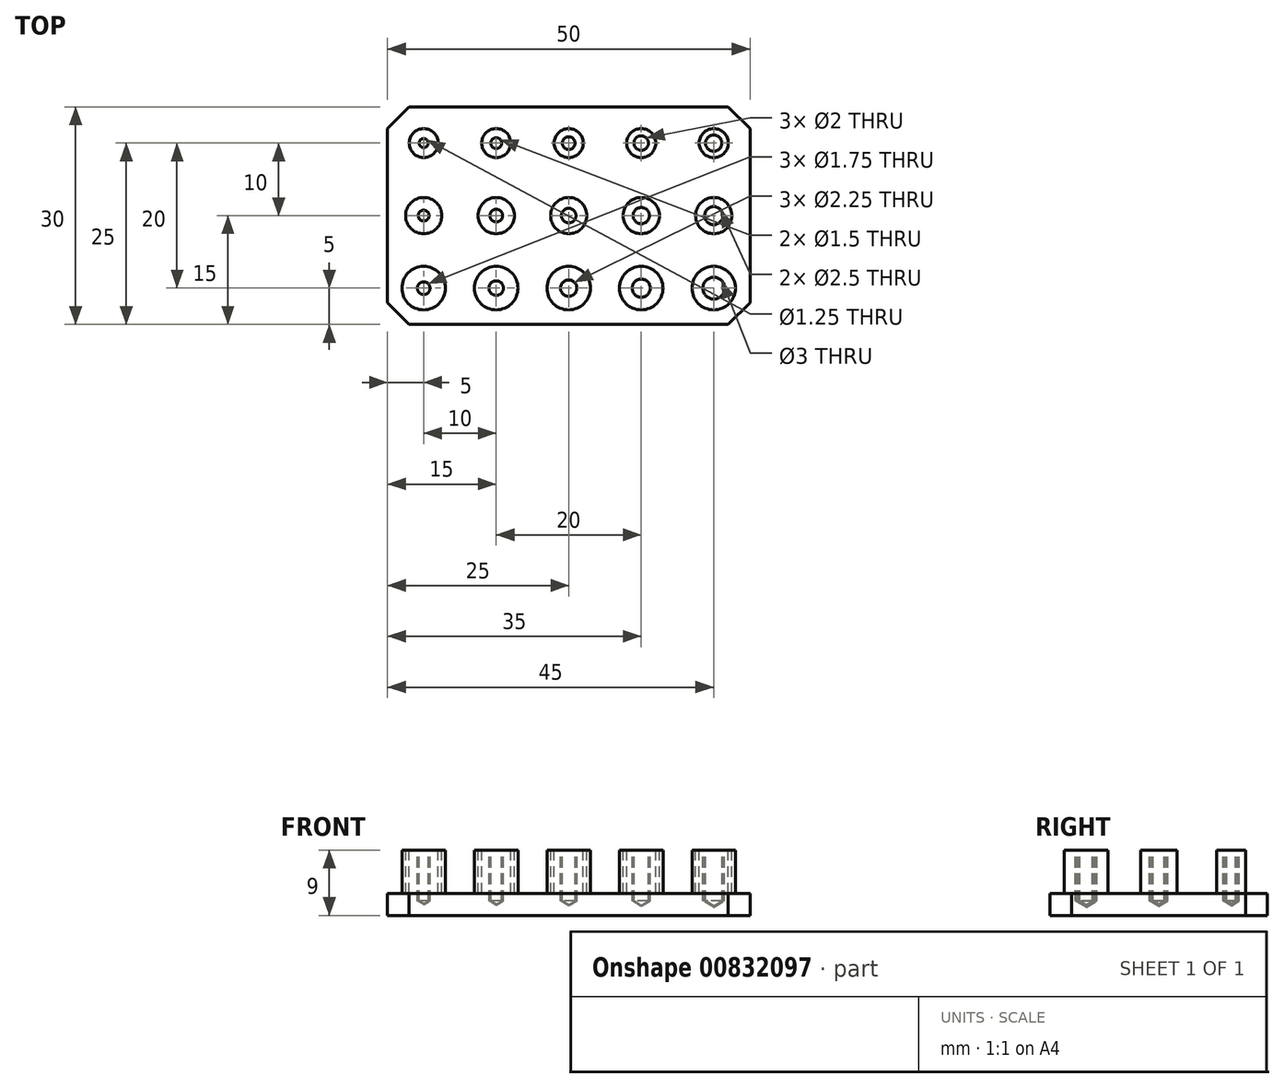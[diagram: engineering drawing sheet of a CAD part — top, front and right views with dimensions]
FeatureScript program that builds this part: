
annotation { "Feature Type Name" : "Feature", "Feature Type Description" : "" }
export const myFeature = defineFeature(function(context is Context, id is Id, definition is map)
    precondition{}
    {
        {
            var Q0;
            Q0=qCreatedBy(makeId("Top.planeOp"),FACE);
            var sketch = newSketch(context, id + "F0", { "sketchPlane" : qUnion([Q0])});
            skLineSegment(sketch, "E0.bottom", {"start": v(-25, 15) * mm, "end": v(25, 15) * mm});
            skLineSegment(sketch, "E0.top", {"start": v(-25, -15) * mm, "end": v(25, -15) * mm});
            skLineSegment(sketch, "E0.left", {"start": v(-25, 15) * mm, "end": v(-25, -15) * mm});
            skLineSegment(sketch, "E0.right", {"start": v(25, 15) * mm, "end": v(25, -15) * mm});
            skSolve(sketch);
        }
        {
            var Q0;
            Q0=makeQuery(id+"F0.imprint","IMPRINT",FACE,{"disambiguationData":[TD([[makeQuery(id+"F0.imprint","IMPRINT",EDGE,{"derivedFrom":sQuery(id+"F0.wireOp",EDGE,"E0.bottom")}),-1.0]])]});
            extrude(context, id + "F1", {"entities" : qUnion([Q0]), "oppositeDirection" : true, "depth" : 3 * mm, "offsetDistance" : 25 * mm});
        }
        {
            var Q0;
            Q0=makeQuery(id+"F1.opExtrude","SWEPT_EDGE",EDGE,{"disambiguationData":[OSD([sQuery(id+"F0.wireOp",EDGE,"E0.top"),sQuery(id+"F0.wireOp",EDGE,"E0.left")])]});
            var Q1;
            Q1=makeQuery(id+"F1.opExtrude","SWEPT_EDGE",EDGE,{"disambiguationData":[OSD([sQuery(id+"F0.wireOp",EDGE,"E0.top"),sQuery(id+"F0.wireOp",EDGE,"E0.right")])]});
            var Q2;
            Q2=makeQuery(id+"F1.opExtrude","SWEPT_EDGE",EDGE,{"disambiguationData":[OSD([sQuery(id+"F0.wireOp",EDGE,"E0.bottom"),sQuery(id+"F0.wireOp",EDGE,"E0.right")])]});
            var Q3;
            Q3=makeQuery(id+"F1.opExtrude","SWEPT_EDGE",EDGE,{"disambiguationData":[OSD([sQuery(id+"F0.wireOp",EDGE,"E0.bottom"),sQuery(id+"F0.wireOp",EDGE,"E0.left")])]});
            chamfer(context, id + "F2", {"entities" : qUnion([Q0, Q1, Q2, Q3]), "width" : 3 * mm, "tangentPropagation" : true});
        }
        {
            var Q0;
            Q0=makeQuery(id+"F1.opExtrude","CAP_FACE",FACE,{"disambiguationData":[OSD([sQuery(id+"F0.wireOp",EDGE,"E0.bottom"),sQuery(id+"F0.wireOp",EDGE,"E0.top"),sQuery(id+"F0.wireOp",EDGE,"E0.left"),sQuery(id+"F0.wireOp",EDGE,"E0.right")])],"isStart":true});
            cPlane(context, id + "F3", {"entities" : qUnion([Q0]), "cplaneType" : CPlaneType.OFFSET, "offset" : 6 * mm, "width" : 150 * mm, "height" : 150 * mm});
        }
        {
            var Q0;
            Q0=qCreatedBy(id+"F3.planeOp",FACE);
            var sketch = newSketch(context, id + "F4", { "sketchPlane" : qUnion([Q0])});
            skPoint(sketch, "E1", {"position": v(10, 0) * mm});
            skPoint(sketch, "E2", {"position": v(20, 0) * mm});
            skPoint(sketch, "E3", {"position": v(0, 0) * mm});
            skPoint(sketch, "E4", {"position": v(-10, 0) * mm});
            skPoint(sketch, "E5", {"position": v(-20, 0) * mm});
            skPoint(sketch, "E6", {"position": v(0, 10) * mm});
            skPoint(sketch, "E7", {"position": v(-10, 10) * mm});
            skPoint(sketch, "E8", {"position": v(-20, 10) * mm});
            skPoint(sketch, "E9", {"position": v(10, 10) * mm});
            skPoint(sketch, "E10", {"position": v(20, 10) * mm});
            skPoint(sketch, "E11", {"position": v(0, -10) * mm});
            skPoint(sketch, "E12", {"position": v(-10, -10) * mm});
            skPoint(sketch, "E13", {"position": v(-20, -10) * mm});
            skPoint(sketch, "E14", {"position": v(10, -10) * mm});
            skPoint(sketch, "E15", {"position": v(20, -10) * mm});
            skCircle(sketch, "E16", {"center": v(-20, 10) * mm, "radius": 2 * mm});
            skCircle(sketch, "E17", {"center": v(-10, 10) * mm, "radius": 2 * mm});
            skCircle(sketch, "E18", {"center": v(0, 10) * mm, "radius": 2 * mm});
            skCircle(sketch, "E19", {"center": v(10, 10) * mm, "radius": 2 * mm});
            skCircle(sketch, "E20", {"center": v(20, 10) * mm, "radius": 2 * mm});
            skCircle(sketch, "E21", {"center": v(-20, 0) * mm, "radius": 2.5 * mm});
            skCircle(sketch, "E22", {"center": v(-10, 0) * mm, "radius": 2.5 * mm});
            skCircle(sketch, "E23", {"center": v(0, 0) * mm, "radius": 2.5 * mm});
            skCircle(sketch, "E24", {"center": v(10, 0) * mm, "radius": 2.5 * mm});
            skCircle(sketch, "E25", {"center": v(20, 0) * mm, "radius": 2.5 * mm});
            skCircle(sketch, "E26", {"center": v(-20, -10) * mm, "radius": 3 * mm});
            skCircle(sketch, "E27", {"center": v(-10, -10) * mm, "radius": 3 * mm});
            skCircle(sketch, "E28", {"center": v(0, -10) * mm, "radius": 3 * mm});
            skCircle(sketch, "E29", {"center": v(10, -10) * mm, "radius": 3 * mm});
            skCircle(sketch, "E30", {"center": v(20, -10) * mm, "radius": 3 * mm});
            skSolve(sketch);
        }
        {
            var Q0;
            Q0=makeQuery(id+"F4.imprint","IMPRINT",FACE,{"disambiguationData":[TD([[makeQuery(id+"F4.imprint","IMPRINT",EDGE,{"derivedFrom":sQuery(id+"F4.wireOp",EDGE,"E21")}),1.0]])]});
            var Q1;
            Q1=makeQuery(id+"F4.imprint","IMPRINT",FACE,{"disambiguationData":[TD([[makeQuery(id+"F4.imprint","IMPRINT",EDGE,{"derivedFrom":sQuery(id+"F4.wireOp",EDGE,"E22")}),1.0]])]});
            var Q2;
            Q2=makeQuery(id+"F4.imprint","IMPRINT",FACE,{"disambiguationData":[TD([[makeQuery(id+"F4.imprint","IMPRINT",EDGE,{"derivedFrom":sQuery(id+"F4.wireOp",EDGE,"E23")}),1.0]])]});
            var Q3;
            Q3=makeQuery(id+"F4.imprint","IMPRINT",FACE,{"disambiguationData":[TD([[makeQuery(id+"F4.imprint","IMPRINT",EDGE,{"derivedFrom":sQuery(id+"F4.wireOp",EDGE,"E24")}),1.0]])]});
            var Q4;
            Q4=makeQuery(id+"F4.imprint","IMPRINT",FACE,{"disambiguationData":[TD([[makeQuery(id+"F4.imprint","IMPRINT",EDGE,{"derivedFrom":sQuery(id+"F4.wireOp",EDGE,"E25")}),1.0]])]});
            var Q5;
            Q5=makeQuery(id+"F4.imprint","IMPRINT",FACE,{"disambiguationData":[TD([[makeQuery(id+"F4.imprint","IMPRINT",EDGE,{"derivedFrom":sQuery(id+"F4.wireOp",EDGE,"E16")}),1.0]])]});
            var Q6;
            Q6=makeQuery(id+"F4.imprint","IMPRINT",FACE,{"disambiguationData":[TD([[makeQuery(id+"F4.imprint","IMPRINT",EDGE,{"derivedFrom":sQuery(id+"F4.wireOp",EDGE,"E17")}),1.0]])]});
            var Q7;
            Q7=makeQuery(id+"F4.imprint","IMPRINT",FACE,{"disambiguationData":[TD([[makeQuery(id+"F4.imprint","IMPRINT",EDGE,{"derivedFrom":sQuery(id+"F4.wireOp",EDGE,"E18")}),1.0]])]});
            var Q8;
            Q8=makeQuery(id+"F4.imprint","IMPRINT",FACE,{"disambiguationData":[TD([[makeQuery(id+"F4.imprint","IMPRINT",EDGE,{"derivedFrom":sQuery(id+"F4.wireOp",EDGE,"E19")}),1.0]])]});
            var Q9;
            Q9=makeQuery(id+"F4.imprint","IMPRINT",FACE,{"disambiguationData":[TD([[makeQuery(id+"F4.imprint","IMPRINT",EDGE,{"derivedFrom":sQuery(id+"F4.wireOp",EDGE,"E20")}),1.0]])]});
            var Q10;
            Q10=makeQuery(id+"F4.imprint","IMPRINT",FACE,{"disambiguationData":[TD([[makeQuery(id+"F4.imprint","IMPRINT",EDGE,{"derivedFrom":sQuery(id+"F4.wireOp",EDGE,"E26")}),1.0]])]});
            var Q11;
            Q11=makeQuery(id+"F4.imprint","IMPRINT",FACE,{"disambiguationData":[TD([[makeQuery(id+"F4.imprint","IMPRINT",EDGE,{"derivedFrom":sQuery(id+"F4.wireOp",EDGE,"E27")}),1.0]])]});
            var Q12;
            Q12=makeQuery(id+"F4.imprint","IMPRINT",FACE,{"disambiguationData":[TD([[makeQuery(id+"F4.imprint","IMPRINT",EDGE,{"derivedFrom":sQuery(id+"F4.wireOp",EDGE,"E28")}),1.0]])]});
            var Q13;
            Q13=makeQuery(id+"F4.imprint","IMPRINT",FACE,{"disambiguationData":[TD([[makeQuery(id+"F4.imprint","IMPRINT",EDGE,{"derivedFrom":sQuery(id+"F4.wireOp",EDGE,"E29")}),1.0]])]});
            var Q14;
            Q14=makeQuery(id+"F4.imprint","IMPRINT",FACE,{"disambiguationData":[TD([[makeQuery(id+"F4.imprint","IMPRINT",EDGE,{"derivedFrom":sQuery(id+"F4.wireOp",EDGE,"E30")}),1.0]])]});
            extrude(context, id + "F5", {"entities" : qUnion([Q0, Q1, Q2, Q3, Q4, Q5, Q6, Q7, Q8, Q9, Q10, Q11, Q12, Q13, Q14]), "operationType" : NewBodyOperationType.ADD, "oppositeDirection" : true, "depth" : 6 * mm, "offsetDistance" : 25 * mm});
        }
        {
            var Q0;
            Q0=sQuery(id+"F4.wireOp",VERTEX,"E3");
            var Q1;
            Q1=sQuery(id+"F4.wireOp",VERTEX,"E9");
            var Q2;
            Q2=sQuery(id+"F4.wireOp",VERTEX,"E12");
            var Q3;
            Q3=makeQuery(id+"F1.opExtrude","SWEPT_BODY",BODY,{"disambiguationData":[OSD([sQuery(id+"F0.wireOp",EDGE,"E0.bottom"),sQuery(id+"F0.wireOp",EDGE,"E0.top"),sQuery(id+"F0.wireOp",EDGE,"E0.left"),sQuery(id+"F0.wireOp",EDGE,"E0.right")])]});
            hole(context, id + "F6", {"style" : HoleStyle.SIMPLE, "endStyle" : HoleEndStyle.BLIND, "holeDiameter" : 2 * mm, "majorDiameter" : 5 * mm, "holeDepth" : 7 * mm, "isTappedThrough" : true, "tappedDepth" : 12 * mm, "tapClearance" : 3, "locations" : qUnion([Q0, Q1, Q2]), "scope" : qUnion([Q3])});
        }
        {
            var Q0;
            Q0=sQuery(id+"F4.wireOp",VERTEX,"E13");
            var Q1;
            Q1=sQuery(id+"F4.wireOp",VERTEX,"E4");
            var Q2;
            Q2=sQuery(id+"F4.wireOp",VERTEX,"E6");
            var Q3;
            Q3=makeQuery(id+"F1.opExtrude","SWEPT_BODY",BODY,{"disambiguationData":[OSD([sQuery(id+"F0.wireOp",EDGE,"E0.bottom"),sQuery(id+"F0.wireOp",EDGE,"E0.top"),sQuery(id+"F0.wireOp",EDGE,"E0.left"),sQuery(id+"F0.wireOp",EDGE,"E0.right")])]});
            hole(context, id + "F7", {"style" : HoleStyle.SIMPLE, "endStyle" : HoleEndStyle.BLIND, "holeDiameter" : 1.75 * mm, "majorDiameter" : 5 * mm, "holeDepth" : 7 * mm, "isTappedThrough" : true, "tappedDepth" : 12 * mm, "tapClearance" : 3, "locations" : qUnion([Q0, Q1, Q2]), "scope" : qUnion([Q3])});
        }
        {
            var Q0;
            Q0=sQuery(id+"F4.wireOp",VERTEX,"E5");
            var Q1;
            Q1=sQuery(id+"F4.wireOp",VERTEX,"E7");
            var Q2;
            Q2=makeQuery(id+"F1.opExtrude","SWEPT_BODY",BODY,{"disambiguationData":[OSD([sQuery(id+"F0.wireOp",EDGE,"E0.bottom"),sQuery(id+"F0.wireOp",EDGE,"E0.top"),sQuery(id+"F0.wireOp",EDGE,"E0.left"),sQuery(id+"F0.wireOp",EDGE,"E0.right")])]});
            hole(context, id + "F8", {"style" : HoleStyle.SIMPLE, "endStyle" : HoleEndStyle.BLIND, "holeDiameter" : 1.5 * mm, "majorDiameter" : 5 * mm, "holeDepth" : 7 * mm, "isTappedThrough" : true, "tappedDepth" : 12 * mm, "tapClearance" : 3, "locations" : qUnion([Q0, Q1]), "scope" : qUnion([Q2])});
        }
        {
            var Q0;
            Q0=sQuery(id+"F4.wireOp",VERTEX,"E8");
            var Q1;
            Q1=makeQuery(id+"F1.opExtrude","SWEPT_BODY",BODY,{"disambiguationData":[OSD([sQuery(id+"F0.wireOp",EDGE,"E0.bottom"),sQuery(id+"F0.wireOp",EDGE,"E0.top"),sQuery(id+"F0.wireOp",EDGE,"E0.left"),sQuery(id+"F0.wireOp",EDGE,"E0.right")])]});
            hole(context, id + "F9", {"style" : HoleStyle.SIMPLE, "endStyle" : HoleEndStyle.BLIND, "holeDiameter" : 1.25 * mm, "majorDiameter" : 5 * mm, "holeDepth" : 7 * mm, "isTappedThrough" : true, "tappedDepth" : 12 * mm, "tapClearance" : 3, "locations" : qUnion([Q0]), "scope" : qUnion([Q1])});
        }
        {
            var Q0;
            Q0=sQuery(id+"F4.wireOp",VERTEX,"E11");
            var Q1;
            Q1=sQuery(id+"F4.wireOp",VERTEX,"E1");
            var Q2;
            Q2=sQuery(id+"F4.wireOp",VERTEX,"E10");
            var Q3;
            Q3=makeQuery(id+"F1.opExtrude","SWEPT_BODY",BODY,{"disambiguationData":[OSD([sQuery(id+"F0.wireOp",EDGE,"E0.bottom"),sQuery(id+"F0.wireOp",EDGE,"E0.top"),sQuery(id+"F0.wireOp",EDGE,"E0.left"),sQuery(id+"F0.wireOp",EDGE,"E0.right")])]});
            hole(context, id + "F10", {"style" : HoleStyle.SIMPLE, "endStyle" : HoleEndStyle.BLIND, "holeDiameter" : 2.25 * mm, "majorDiameter" : 5 * mm, "holeDepth" : 7 * mm, "isTappedThrough" : true, "tappedDepth" : 12 * mm, "tapClearance" : 3, "locations" : qUnion([Q0, Q1, Q2]), "scope" : qUnion([Q3])});
        }
        {
            var Q0;
            Q0=sQuery(id+"F4.wireOp",VERTEX,"E14");
            var Q1;
            Q1=sQuery(id+"F4.wireOp",VERTEX,"E2");
            var Q2;
            Q2=makeQuery(id+"F1.opExtrude","SWEPT_BODY",BODY,{"disambiguationData":[OSD([sQuery(id+"F0.wireOp",EDGE,"E0.bottom"),sQuery(id+"F0.wireOp",EDGE,"E0.top"),sQuery(id+"F0.wireOp",EDGE,"E0.left"),sQuery(id+"F0.wireOp",EDGE,"E0.right")])]});
            hole(context, id + "F11", {"style" : HoleStyle.SIMPLE, "endStyle" : HoleEndStyle.BLIND, "holeDiameter" : 2.5 * mm, "majorDiameter" : 5 * mm, "holeDepth" : 7 * mm, "isTappedThrough" : true, "tappedDepth" : 12 * mm, "tapClearance" : 3, "locations" : qUnion([Q0, Q1]), "scope" : qUnion([Q2])});
        }
        {
            var Q0;
            Q0=sQuery(id+"F4.wireOp",VERTEX,"E15");
            var Q1;
            Q1=makeQuery(id+"F1.opExtrude","SWEPT_BODY",BODY,{"disambiguationData":[OSD([sQuery(id+"F0.wireOp",EDGE,"E0.bottom"),sQuery(id+"F0.wireOp",EDGE,"E0.top"),sQuery(id+"F0.wireOp",EDGE,"E0.left"),sQuery(id+"F0.wireOp",EDGE,"E0.right")])]});
            hole(context, id + "F12", {"style" : HoleStyle.SIMPLE, "endStyle" : HoleEndStyle.BLIND, "holeDiameter" : 3 * mm, "majorDiameter" : 5 * mm, "holeDepth" : 7 * mm, "isTappedThrough" : true, "tappedDepth" : 12 * mm, "tapClearance" : 3, "locations" : qUnion([Q0]), "scope" : qUnion([Q1])});
        }
    });
